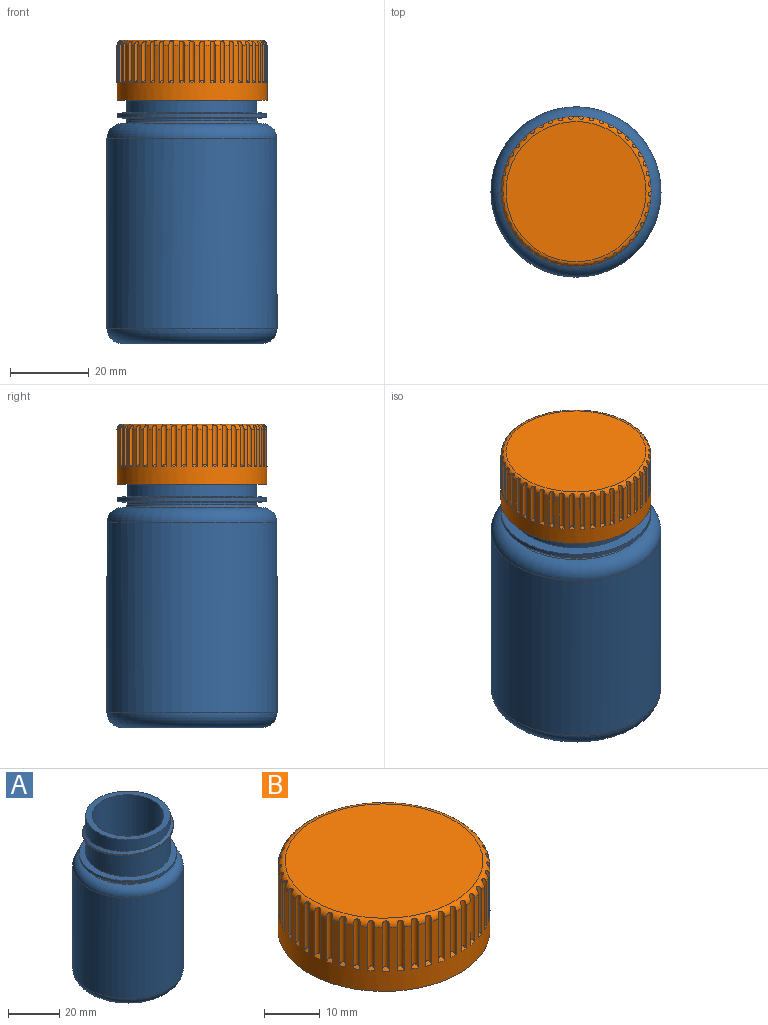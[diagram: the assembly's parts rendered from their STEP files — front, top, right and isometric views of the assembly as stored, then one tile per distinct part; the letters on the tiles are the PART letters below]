
ASSEMBLY  parts=2 mates=1
PART A: 24 faces, bbox 46.8x46.8x76.2 mm
  f0: plane 1.31x1.28mm, normal (0,1,0), area 1mm2, adj f2,f3,f4,f5
  f1: plane 1.31x1.27mm, normal (0,-1,0), area 1mm2, adj f2,f3,f4,f5
  f2: bspline ~36.58x36.58mm, area 105.4mm2, adj f0,f1,f4,f5
  f3: bspline ~36.58x36.58mm, area 149.4mm2, adj f0,f1,f4,f5
  f4: bspline ~36.58x36.58mm, area 71.3mm2, adj f0,f1,f2,f3
  f5: cylinder r=16.51mm len=33.02mm, axis (0,0,-1), area 1686.3mm2, adj f0,f1,f2,f3,f6,f16
  f6: plane 33.02x33.02mm, normal (0,0,1), area 243.2mm2, adj f5,f17
  f7: cylinder r=16.51mm len=33.02mm, axis (0,0,-1), area 65.9mm2, adj f13,f15
  f8: plane 35.56x35.56mm, normal (0,0,1), area 69.7mm2, adj f11,f13
  f9: cylinder r=21.59mm len=48.26mm, axis (0,0,-1), area 6546.7mm2, adj f11,f12
  f10: plane 35.56x35.56mm, normal (0,0,-1), area 993.1mm2, adj f12
  f11: torus R=17.78mm, axis (0,0,-1), area 759.8mm2, adj f8,f9
  f12: torus R=17.78mm, axis (0,0,1), area 759.8mm2, adj f9,f10
  f13: torus R=17.14mm, axis (0,0,-1), area 104.9mm2, adj f7,f8
  f14: cylinder r=19.04mm len=38.07mm, axis (0,0,-1), area 121.5mm2, adj f15,f16
  f15: cone r=16.51mm half-angle=84.3deg, axis (0,0,1), area 283.7mm2, adj f7,f14
  f16: cone r=19.04mm half-angle=84.3deg, axis (0,0,-1), area 283.7mm2, adj f5,f14
  f17: cylinder r=13.97mm len=27.94mm, axis (0,0,-1), area 1727.9mm2, adj f6,f23
  f18: plane 35.56x35.56mm, normal (0,0,-1), area 69.7mm2, adj f21,f23
  f19: cylinder r=19.05mm len=48.26mm, axis (0,0,-1), area 5776.5mm2, adj f21,f22
  f20: plane 35.56x35.56mm, normal (0,0,1), area 993.1mm2, adj f22
  f21: torus R=17.78mm, axis (0,0,-1), area 233mm2, adj f18,f19
  f22: torus R=17.78mm, axis (0,0,1), area 233mm2, adj f19,f20
  f23: torus R=17.14mm, axis (0,0,-1), area 473.9mm2, adj f17,f18
PART B: 100 faces, bbox 41.2x41.2x15.2 mm
  f0: plane 38.1x38.1mm, normal (0,0,-1), area 283.8mm2, adj f1,f4
  f1: cylinder r=19.05mm len=38.1mm, axis (0,0,-1), area 1127.8mm2, adj f0,f3,f10,f11,f12,f13,f14,f15
  f2: plane 35.56x35.56mm, normal (0,0,1), area 993.1mm2, adj f3
  f3: torus R=17.78mm, axis (0,0,-1), area 166.9mm2, adj f1,f2,f10,f11,f12,f13,f14,f15
  f4: cylinder r=16.51mm len=33.02mm, axis (0,0,-1), area 1053.9mm2, adj f0,f5,f6,f7,f8,f9
  f5: plane 33.02x33.02mm, normal (0,0,-1), area 856.3mm2, adj f4
  f6: plane 1.27x1.1mm, normal (0,1,0), area 0.7mm2, adj f4,f8,f9
  f7: plane 1.27x1.1mm, normal (0,-1,0), area 0.7mm2, adj f4,f8,f9
  f8: bspline ~33.02x33.02mm, area 127.9mm2, adj f4,f6,f7,f9
  f9: bspline ~33.02x33.02mm, area 127.9mm2, adj f4,f6,f7,f8
  f10: cylinder r=0.64mm len=10.63mm, axis (0,0,1), area 19.7mm2, adj f1,f3,f80
  f11: cylinder r=0.64mm len=10.63mm, axis (0,0,1), area 19.7mm2, adj f1,f3,f81
  f12: cylinder r=0.64mm len=10.63mm, axis (0,0,1), area 19.7mm2, adj f1,f3,f82
  f13: cylinder r=0.64mm len=10.63mm, axis (0,0,1), area 19.7mm2, adj f1,f3,f83
  f14: cylinder r=0.64mm len=10.63mm, axis (0,0,1), area 19.7mm2, adj f1,f3,f84
  f15: cylinder r=0.64mm len=10.63mm, axis (0,0,1), area 19.7mm2, adj f1,f3,f85
  f16: cylinder r=0.64mm len=10.63mm, axis (0,0,1), area 19.7mm2, adj f1,f3,f86
  f17: cylinder r=0.64mm len=10.63mm, axis (0,0,1), area 19.7mm2, adj f1,f3,f87
  f18: cylinder r=0.64mm len=10.63mm, axis (0,0,1), area 19.7mm2, adj f1,f3,f88
  f19: cylinder r=0.64mm len=10.63mm, axis (0,0,1), area 19.7mm2, adj f1,f3,f89
  f20: cylinder r=0.64mm len=10.63mm, axis (0,0,1), area 19.7mm2, adj f1,f3,f90
  f21: cylinder r=0.64mm len=10.63mm, axis (0,0,1), area 19.7mm2, adj f1,f3,f91
  f22: cylinder r=0.64mm len=10.63mm, axis (0,0,1), area 19.7mm2, adj f1,f3,f92
  f23: cylinder r=0.64mm len=10.63mm, axis (0,0,1), area 19.7mm2, adj f1,f3,f79
  f24: cylinder r=0.64mm len=10.63mm, axis (0,0,1), area 19.7mm2, adj f1,f3,f78
  f25: cylinder r=0.64mm len=10.63mm, axis (0,0,1), area 19.7mm2, adj f1,f3,f77
  f26: cylinder r=0.64mm len=10.63mm, axis (0,0,1), area 19.7mm2, adj f1,f3,f76
  f27: cylinder r=0.64mm len=10.63mm, axis (0,0,1), area 19.7mm2, adj f1,f3,f75
  f28: cylinder r=0.64mm len=10.63mm, axis (0,0,1), area 19.7mm2, adj f1,f3,f74
  f29: cylinder r=0.64mm len=10.63mm, axis (0,0,1), area 19.7mm2, adj f1,f3,f73
  f30: cylinder r=0.64mm len=10.63mm, axis (0,0,1), area 19.7mm2, adj f1,f3,f72
  f31: cylinder r=0.64mm len=10.63mm, axis (0,0,1), area 19.7mm2, adj f1,f3,f71
  f32: cylinder r=0.64mm len=10.63mm, axis (0,0,1), area 19.7mm2, adj f1,f3,f70
  f33: cylinder r=0.64mm len=10.63mm, axis (0,0,1), area 19.7mm2, adj f1,f3,f69
  f34: cylinder r=0.64mm len=10.63mm, axis (0,0,1), area 19.7mm2, adj f1,f3,f68
  f35: cylinder r=0.64mm len=10.63mm, axis (0,0,1), area 19.7mm2, adj f1,f3,f67
  f36: cylinder r=0.64mm len=10.63mm, axis (0,0,1), area 19.7mm2, adj f1,f3,f66
  f37: cylinder r=0.64mm len=10.63mm, axis (0,0,1), area 19.7mm2, adj f1,f3,f65
  f38: cylinder r=0.64mm len=10.63mm, axis (0,0,1), area 19.7mm2, adj f1,f3,f64
  f39: cylinder r=0.64mm len=10.63mm, axis (0,0,1), area 19.7mm2, adj f1,f3,f63
  f40: cylinder r=0.64mm len=10.63mm, axis (0,0,1), area 19.7mm2, adj f1,f3,f62
  f41: cylinder r=0.64mm len=10.63mm, axis (0,0,1), area 19.7mm2, adj f1,f3,f61
  f42: cylinder r=0.64mm len=10.63mm, axis (0,0,1), area 19.7mm2, adj f1,f3,f60
  f43: cylinder r=0.64mm len=10.63mm, axis (0,0,1), area 19.7mm2, adj f1,f3,f59
  f44: cylinder r=0.64mm len=10.63mm, axis (0,0,1), area 19.7mm2, adj f1,f3,f58
  f45: cylinder r=0.64mm len=10.63mm, axis (0,0,1), area 19.7mm2, adj f1,f3,f57
  f46: cylinder r=0.64mm len=10.63mm, axis (0,0,1), area 19.7mm2, adj f1,f3,f56
  f47: cylinder r=0.64mm len=10.63mm, axis (0,0,1), area 19.7mm2, adj f1,f3,f55
  f48: cylinder r=0.64mm len=10.63mm, axis (0,0,1), area 19.7mm2, adj f1,f3,f99
  f49: cylinder r=0.64mm len=10.63mm, axis (0,0,1), area 19.7mm2, adj f1,f3,f98
  f50: cylinder r=0.64mm len=10.63mm, axis (0,0,1), area 19.7mm2, adj f1,f3,f97
  f51: cylinder r=0.64mm len=10.63mm, axis (0,0,1), area 19.7mm2, adj f1,f3,f96
  f52: cylinder r=0.64mm len=10.63mm, axis (0,0,1), area 19.7mm2, adj f1,f3,f95
  f53: cylinder r=0.64mm len=10.63mm, axis (0,0,1), area 19.7mm2, adj f1,f3,f94
  f54: cylinder r=0.64mm len=10.63mm, axis (0,0,1), area 19.7mm2, adj f1,f3,f93
  f55: cone r=18.41mm half-angle=45deg, axis (0,0,-1), area 0.9mm2, adj f1,f47
  f56: cone r=18.41mm half-angle=45deg, axis (0,0,-1), area 0.9mm2, adj f1,f46
  f57: cone r=18.41mm half-angle=45deg, axis (0,0,-1), area 0.9mm2, adj f1,f45
  f58: cone r=18.41mm half-angle=45deg, axis (0,0,-1), area 0.9mm2, adj f1,f44
  f59: cone r=18.41mm half-angle=45deg, axis (0,0,-1), area 0.9mm2, adj f1,f43
  f60: cone r=18.41mm half-angle=45deg, axis (0,0,-1), area 0.9mm2, adj f1,f42
  f61: cone r=18.41mm half-angle=45deg, axis (0,0,-1), area 0.9mm2, adj f1,f41
  f62: cone r=18.41mm half-angle=45deg, axis (0,0,-1), area 0.9mm2, adj f1,f40
  f63: cone r=18.41mm half-angle=45deg, axis (0,0,-1), area 0.9mm2, adj f1,f39
  f64: cone r=18.41mm half-angle=45deg, axis (0,0,-1), area 0.9mm2, adj f1,f38
  f65: cone r=18.41mm half-angle=45deg, axis (0,0,-1), area 0.9mm2, adj f1,f37
  f66: cone r=18.41mm half-angle=45deg, axis (0,0,-1), area 0.9mm2, adj f1,f36
  f67: cone r=18.41mm half-angle=45deg, axis (0,0,-1), area 0.9mm2, adj f1,f35
  f68: cone r=18.41mm half-angle=45deg, axis (0,0,-1), area 0.9mm2, adj f1,f34
  f69: cone r=18.41mm half-angle=45deg, axis (0,0,-1), area 0.9mm2, adj f1,f33
  f70: cone r=18.41mm half-angle=45deg, axis (0,0,-1), area 0.9mm2, adj f1,f32
  f71: cone r=18.41mm half-angle=45deg, axis (0,0,-1), area 0.9mm2, adj f1,f31
  f72: cone r=18.41mm half-angle=45deg, axis (0,0,-1), area 0.9mm2, adj f1,f30
  f73: cone r=18.41mm half-angle=45deg, axis (0,0,-1), area 0.9mm2, adj f1,f29
  f74: cone r=18.41mm half-angle=45deg, axis (0,0,-1), area 0.9mm2, adj f1,f28
  f75: cone r=18.41mm half-angle=45deg, axis (0,0,-1), area 0.9mm2, adj f1,f27
  f76: cone r=18.41mm half-angle=45deg, axis (0,0,-1), area 0.9mm2, adj f1,f26
  f77: cone r=18.41mm half-angle=45deg, axis (0,0,-1), area 0.9mm2, adj f1,f25
  f78: cone r=18.41mm half-angle=45deg, axis (0,0,-1), area 0.9mm2, adj f1,f24
  f79: cone r=18.41mm half-angle=45deg, axis (0,0,-1), area 0.9mm2, adj f1,f23
  f80: cone r=18.41mm half-angle=45deg, axis (0,0,-1), area 0.9mm2, adj f1,f10
  f81: cone r=18.41mm half-angle=45deg, axis (0,0,-1), area 0.9mm2, adj f1,f11
  f82: cone r=18.41mm half-angle=45deg, axis (0,0,-1), area 0.9mm2, adj f1,f12
  f83: cone r=18.41mm half-angle=45deg, axis (0,0,-1), area 0.9mm2, adj f1,f13
  f84: cone r=18.41mm half-angle=45deg, axis (0,0,-1), area 0.9mm2, adj f1,f14
  f85: cone r=18.41mm half-angle=45deg, axis (0,0,-1), area 0.9mm2, adj f1,f15
  f86: cone r=18.41mm half-angle=45deg, axis (0,0,-1), area 0.9mm2, adj f1,f16
  f87: cone r=18.41mm half-angle=45deg, axis (0,0,-1), area 0.9mm2, adj f1,f17
  f88: cone r=18.41mm half-angle=45deg, axis (0,0,-1), area 0.9mm2, adj f1,f18
  f89: cone r=18.41mm half-angle=45deg, axis (0,0,-1), area 0.9mm2, adj f1,f19
  f90: cone r=18.41mm half-angle=45deg, axis (0,0,-1), area 0.9mm2, adj f1,f20
  f91: cone r=18.41mm half-angle=45deg, axis (0,0,-1), area 0.9mm2, adj f1,f21
  f92: cone r=18.41mm half-angle=45deg, axis (0,0,-1), area 0.9mm2, adj f1,f22
  f93: cone r=18.41mm half-angle=45deg, axis (0,0,-1), area 0.9mm2, adj f1,f54
  f94: cone r=18.41mm half-angle=45deg, axis (0,0,-1), area 0.9mm2, adj f1,f53
  f95: cone r=18.41mm half-angle=45deg, axis (0,0,-1), area 0.9mm2, adj f1,f52
  f96: cone r=18.41mm half-angle=45deg, axis (0,0,-1), area 0.9mm2, adj f1,f51
  f97: cone r=18.41mm half-angle=45deg, axis (0,0,-1), area 0.9mm2, adj f1,f50
  f98: cone r=18.41mm half-angle=45deg, axis (0,0,-1), area 0.9mm2, adj f1,f49
  f99: cone r=18.41mm half-angle=45deg, axis (0,0,-1), area 0.9mm2, adj f1,f48
PLACE A t=(-18.78,16,-19.09)mm fixed
PLACE B rot(axis=(0,0,-1),180deg) t=(-18.78,16,42.63)mm
MATE cylindrical A.f5 <-> B.f1  axis (0,0,-1) through (-18.78,16,48.35)mm
